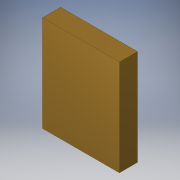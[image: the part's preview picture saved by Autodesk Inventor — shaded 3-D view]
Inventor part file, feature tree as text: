
AUTODESK INVENTOR PART (.ipt)
format: ipt  version: 2017 (Build 210142000, 142)  size: 90,112 bytes
history: native  units: in
note: dims shown in document units (in); Inventor stores cm internally (conversion verified against a paired STEP export)
features: extrude x1, sketch x1
ambient origin geometry x8: Origin, YZ Plane, XZ Plane, XY Plane, X Axis, Y Axis, Z Axis, Center Point
bodies: Solid1 (feature_tree)
feature tree (2):
  extrude  "Extrusion1"  Depth=10.0in
  sketch  "Sketch1"  dims[d0=8.0in d1=10.0in d2=1.88in d3=0.0in]
